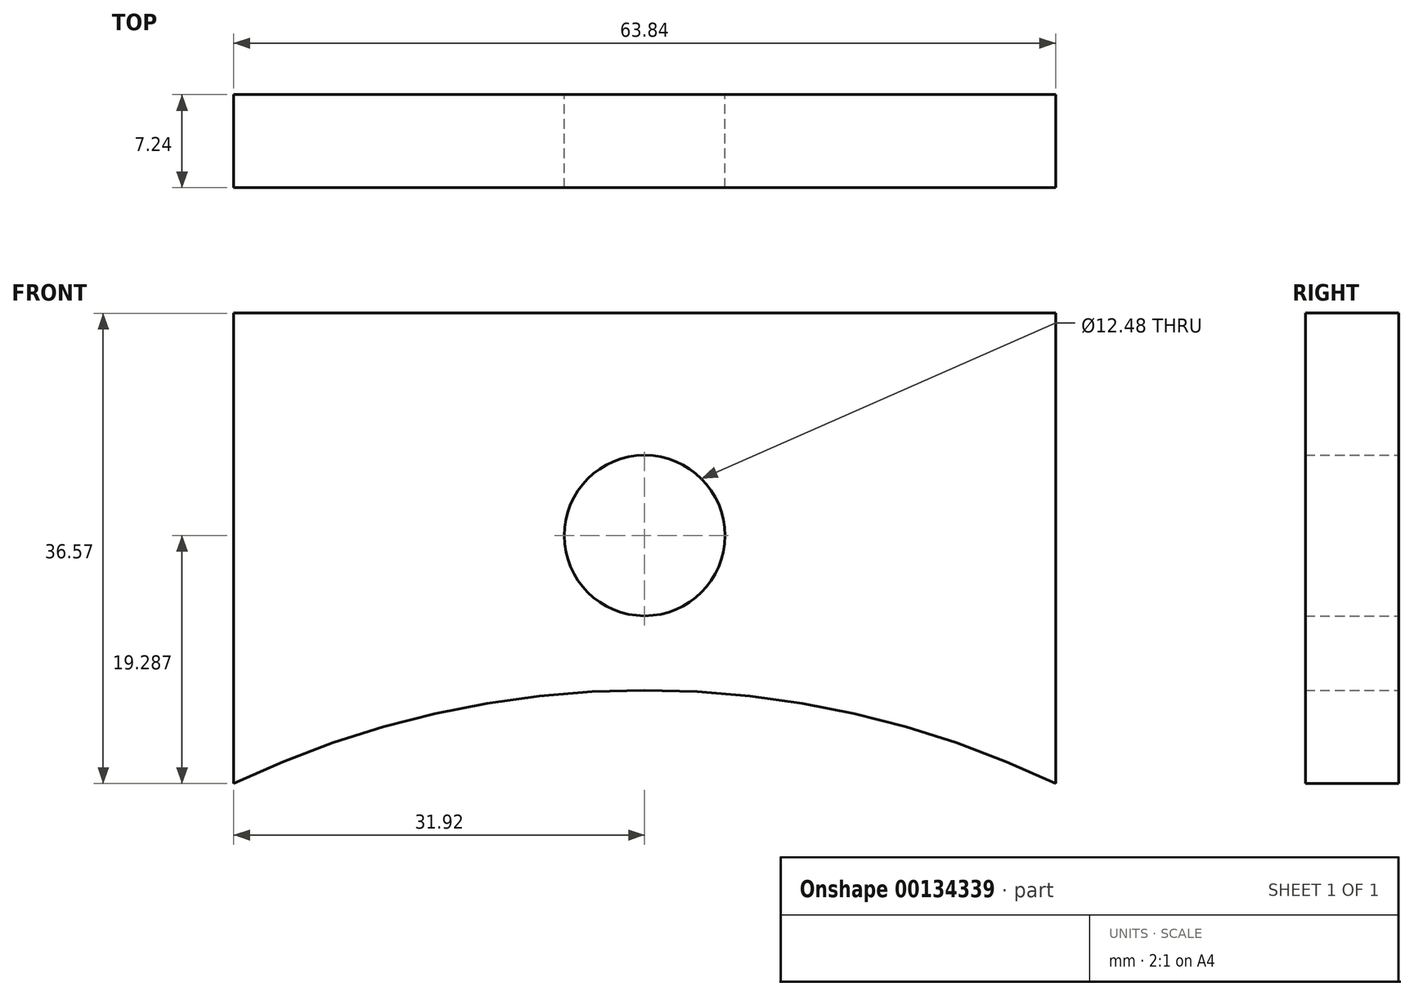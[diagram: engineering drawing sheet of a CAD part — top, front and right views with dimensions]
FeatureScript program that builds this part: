
annotation { "Feature Type Name" : "Feature", "Feature Type Description" : "" }
export const myFeature = defineFeature(function(context is Context, id is Id, definition is map)
    precondition{}
    {
        {
            var Q0;
            Q0=qCreatedBy(makeId("Front.planeOp"),FACE);
            var sketch = newSketch(context, id + "F0", { "sketchPlane" : qUnion([Q0])});
            skLineSegment(sketch, "E0", {"start": v(-31.92, 29.03) * mm, "end": v(-31.92, -7.54) * mm});
            skLineSegment(sketch, "E1", {"start": v(-31.92, 29.03) * mm, "end": v(0, 29.03) * mm});
            skLineSegment(sketch, "E2.MirrorCS", {"start": v(31.92, 29.03) * mm, "end": v(0, 29.03) * mm});
            skLineSegment(sketch, "E3.MirrorCS", {"start": v(31.92, 29.03) * mm, "end": v(31.92, -7.54) * mm});
            skArc(sketch, "E4", {"start": v(31.92, -7.54) * mm, "mid": v(0, -0.28) * mm, "end": v(-31.92, -7.54) * mm});
            skCircle(sketch, "E5", {"center": v(0, 11.75) * mm, "radius": 6.24 * mm});
            skSolve(sketch);
        }
        {
            var Q0;
            Q0=makeQuery(id+"F0.imprint","IMPRINT",FACE,{"disambiguationData":[TD([[makeQuery(id+"F0.imprint","IMPRINT",EDGE,{"derivedFrom":sQuery(id+"F0.wireOp",EDGE,"E0")}),1.0]])]});
            extrude(context, id + "F1", {"entities" : qUnion([Q0]), "depth" : 7.24 * mm});
        }
    });
